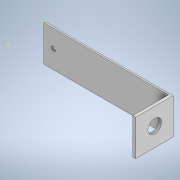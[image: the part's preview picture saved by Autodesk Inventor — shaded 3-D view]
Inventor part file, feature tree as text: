
AUTODESK INVENTOR PART (.ipt)
format: ipt  version: 2020 (Build 240168000, 168)  size: 146,944 bytes
history: native  units: in
note: dims shown in document units (in); Inventor stores cm internally (conversion verified against a paired STEP export)
features: sketch x10, extrude x5, hole x3
ambient origin geometry x8: Origin, YZ Plane, XZ Plane, XY Plane, X Axis, Y Axis, Z Axis, Center Point
bodies: Solid1 (feature_tree)
feature tree (18):
  extrude  "Extrusion1"  Depth=1.6535in TaperAngle=0.0deg
  sketch  "Sketch3"  dims[d28=0.625in d29=0.625in d30=0.75in d31=0.188in d32=90.0deg d33=1.029in d34=0.8108in d35=1.6535in d36=0.0in]
  hole  "Hole4"  [1 undecoded]
  extrude  "Extrusion4"  Depth=2.0in TaperAngle=0.0deg
  extrude  "Extrusion5"  Depth=1.9in TaperAngle=0.0deg
  hole  "Hole5"  [1 undecoded]
  extrude  "Extrusion6"  [1 undecoded]
  sketch  "Sketch13"
  hole  "Hole6"  [1 undecoded]
  extrude  "Extrusion7"  [1 undecoded]
  sketch  "Sketch15"
  sketch  "Sketch1"  dims[d0=1.6535in d1=3.937in d2=0.0in]
  sketch  "Sketch8"  dims[d37=1.0in d38=0.0in]
  sketch  "Sketch9"  dims[d39=0.1969in d40=0.75in d41=0.375in d42=0.25in d43=0.5635in d44=1.0in d45=0.8108in d46=2.0in d47=0.0in]
  sketch  "Sketch10"  dims[d48=0.625in d49=0.75in d50=0.375in d51=0.25in d52=0.5635in d53=1.0in d54=0.8108in d55=1.9in d56=0.0in]
  sketch  "Sketch11"
  sketch  "Sketch12"
  sketch  "Sketch14"
note: 5 required parameter values undecoded (feature->parameter linkage not recoverable at this tier; creation-order binding heuristic only, values carry confidence <= 0.55)
